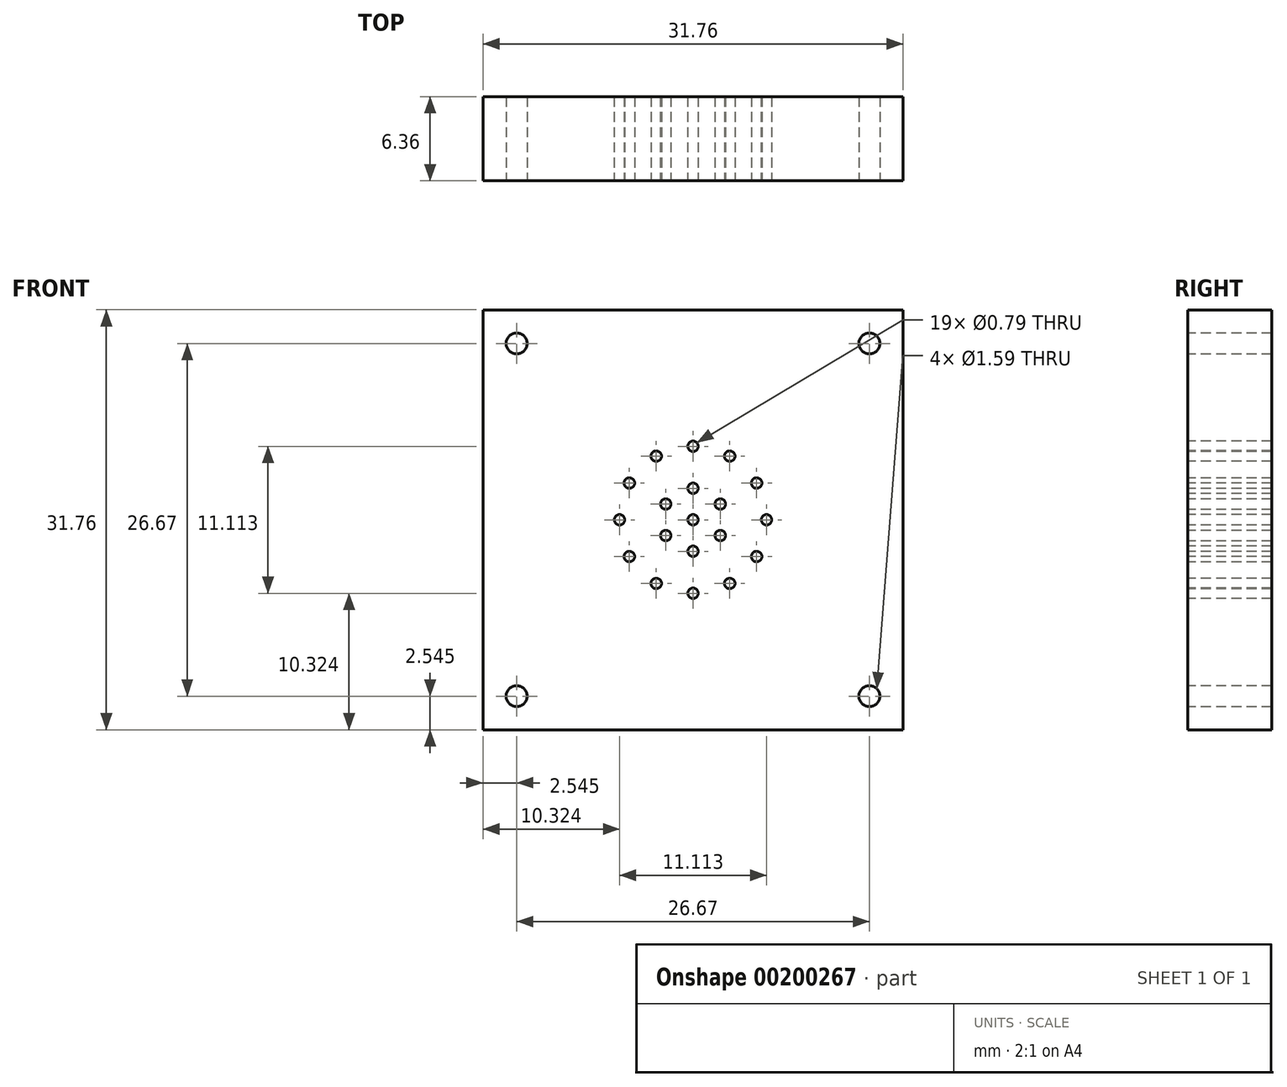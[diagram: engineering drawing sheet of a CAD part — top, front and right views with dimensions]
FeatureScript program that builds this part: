
annotation { "Feature Type Name" : "Feature", "Feature Type Description" : "" }
export const myFeature = defineFeature(function(context is Context, id is Id, definition is map)
    precondition{}
    {
        {
            var Q0;
            Q0=qCreatedBy(makeId("Front.planeOp"),FACE);
            var sketch = newSketch(context, id + "F0", { "sketchPlane" : qUnion([Q0])});
            skLineSegment(sketch, "E0.bottom", {"start": v(15.88, -15.87) * mm, "end": v(-15.88, -15.88) * mm});
            skLineSegment(sketch, "E0.top", {"start": v(15.88, 15.88) * mm, "end": v(-15.88, 15.87) * mm});
            skLineSegment(sketch, "E0.left", {"start": v(15.88, -15.88) * mm, "end": v(15.88, 15.88) * mm});
            skLineSegment(sketch, "E0.right", {"start": v(-15.88, -15.88) * mm, "end": v(-15.88, 15.87) * mm});
            skPoint(sketch, "E0.middle", {"position": v(0, 0) * mm});
            skSolve(sketch);
        }
        {
            var Q0;
            Q0=makeQuery(id+"F0.imprint","IMPRINT",FACE,{"disambiguationData":[TD([[makeQuery(id+"F0.imprint","IMPRINT",EDGE,{"derivedFrom":sQuery(id+"F0.wireOp",EDGE,"E0.bottom")}),-1.0]])]});
            extrude(context, id + "F1", {"entities" : qUnion([Q0]), "endBound" : BoundingType.SYMMETRIC, "offsetDistance" : 25.4 * mm, "depth" : 6.35 * mm});
        }
        {
            var Q0;
            Q0=makeQuery(id+"F1.opExtrude","CAP_FACE",FACE,{"disambiguationData":[OSD([sQuery(id+"F0.wireOp",EDGE,"E0.bottom"),sQuery(id+"F0.wireOp",EDGE,"E0.top"),sQuery(id+"F0.wireOp",EDGE,"E0.left"),sQuery(id+"F0.wireOp",EDGE,"E0.right")])],"isStart":false});
            var sketch = newSketch(context, id + "F2", { "sketchPlane" : qUnion([Q0])});
            skCircle(sketch, "E1", {"center": v(0, 0) * mm, "radius": 2.38 * mm});
            skCircle(sketch, "E2", {"center": v(0, 0) * mm, "radius": 5.56 * mm});
            skCircle(sketch, "E3.cCircle", {"center": v(0, 0) * mm, "radius": 2.38 * mm, "construction": true});
            skLineSegment(sketch, "E3.0", {"start": v(0, 2.38) * mm, "end": v(2.06, 1.2) * mm});
            skLineSegment(sketch, "E3.1", {"start": v(2.06, 1.2) * mm, "end": v(2.06, -1.2) * mm});
            skLineSegment(sketch, "E3.2", {"start": v(2.06, -1.2) * mm, "end": v(0, -2.38) * mm});
            skLineSegment(sketch, "E3.3", {"start": v(0, -2.38) * mm, "end": v(-2.06, -1.2) * mm});
            skLineSegment(sketch, "E3.4", {"start": v(-2.06, -1.2) * mm, "end": v(-2.06, 1.2) * mm});
            skLineSegment(sketch, "E3.5", {"start": v(-2.06, 1.2) * mm, "end": v(0, 2.38) * mm});
            skCircle(sketch, "E4.cCircle", {"center": v(0, 0) * mm, "radius": 5.56 * mm, "construction": true});
            skLineSegment(sketch, "E5.0", {"start": v(0, 5.56) * mm, "end": v(2.78, 4.81) * mm});
            skLineSegment(sketch, "E5.1", {"start": v(2.78, 4.81) * mm, "end": v(4.81, 2.78) * mm});
            skLineSegment(sketch, "E5.2", {"start": v(4.81, 2.78) * mm, "end": v(5.56, 0) * mm});
            skLineSegment(sketch, "E5.3", {"start": v(5.56, 0) * mm, "end": v(4.81, -2.78) * mm});
            skLineSegment(sketch, "E5.4", {"start": v(4.81, -2.78) * mm, "end": v(2.78, -4.81) * mm});
            skLineSegment(sketch, "E5.5", {"start": v(2.78, -4.81) * mm, "end": v(0, -5.56) * mm});
            skLineSegment(sketch, "E5.6", {"start": v(0, -5.56) * mm, "end": v(-2.78, -4.81) * mm});
            skLineSegment(sketch, "E5.7", {"start": v(-2.78, -4.81) * mm, "end": v(-4.81, -2.78) * mm});
            skLineSegment(sketch, "E5.8", {"start": v(-4.81, -2.78) * mm, "end": v(-5.56, 0) * mm});
            skLineSegment(sketch, "E5.9", {"start": v(-5.56, 0) * mm, "end": v(-4.81, 2.78) * mm});
            skLineSegment(sketch, "E5.10", {"start": v(-4.81, 2.78) * mm, "end": v(-2.78, 4.81) * mm});
            skLineSegment(sketch, "E5.11", {"start": v(-2.78, 4.81) * mm, "end": v(0, 5.56) * mm});
            skSolve(sketch);
        }
        {
            var Q0;
            Q0=sQuery(id+"F2.wireOp",VERTEX,"E1.center");
            var Q1;
            Q1=sQuery(id+"F2.wireOp",VERTEX,"E3.0.start");
            var Q2;
            Q2=sQuery(id+"F2.wireOp",VERTEX,"E3.1.start");
            var Q3;
            Q3=sQuery(id+"F2.wireOp",VERTEX,"E3.2.start");
            var Q4;
            Q4=sQuery(id+"F2.wireOp",VERTEX,"E3.3.start");
            var Q5;
            Q5=sQuery(id+"F2.wireOp",VERTEX,"E3.4.start");
            var Q6;
            Q6=sQuery(id+"F2.wireOp",VERTEX,"E3.5.start");
            var Q7;
            Q7=sQuery(id+"F2.wireOp",VERTEX,"E4.5.end");
            var Q8;
            Q8=sQuery(id+"F2.wireOp",VERTEX,"E4.1.start");
            var Q9;
            Q9=sQuery(id+"F2.wireOp",VERTEX,"E4.2.start");
            var Q10;
            Q10=sQuery(id+"F2.wireOp",VERTEX,"E4.3.start");
            var Q11;
            Q11=sQuery(id+"F2.wireOp",VERTEX,"E4.4.start");
            var Q12;
            Q12=sQuery(id+"F2.wireOp",VERTEX,"E4.5.start");
            var Q13;
            Q13=sQuery(id+"F2.wireOp",VERTEX,"E5.9.end");
            var Q14;
            Q14=sQuery(id+"F2.wireOp",VERTEX,"E5.11.start");
            var Q15;
            Q15=sQuery(id+"F2.wireOp",VERTEX,"E5.11.end");
            var Q16;
            Q16=sQuery(id+"F2.wireOp",VERTEX,"E5.1.start");
            var Q17;
            Q17=sQuery(id+"F2.wireOp",VERTEX,"E5.2.start");
            var Q18;
            Q18=sQuery(id+"F2.wireOp",VERTEX,"E5.3.start");
            var Q19;
            Q19=sQuery(id+"F2.wireOp",VERTEX,"E5.4.start");
            var Q20;
            Q20=sQuery(id+"F2.wireOp",VERTEX,"E5.5.start");
            var Q21;
            Q21=sQuery(id+"F2.wireOp",VERTEX,"E5.6.start");
            var Q22;
            Q22=sQuery(id+"F2.wireOp",VERTEX,"E5.7.start");
            var Q23;
            Q23=sQuery(id+"F2.wireOp",VERTEX,"E5.8.start");
            var Q24;
            Q24=sQuery(id+"F2.wireOp",VERTEX,"E5.8.end");
            var Q25;
            Q25=makeQuery(id+"F1.opExtrude","SWEPT_BODY",BODY,{"disambiguationData":[OSD([sQuery(id+"F0.wireOp",EDGE,"E0.bottom"),sQuery(id+"F0.wireOp",EDGE,"E0.top"),sQuery(id+"F0.wireOp",EDGE,"E0.left"),sQuery(id+"F0.wireOp",EDGE,"E0.right")])]});
            hole(context, id + "F3", {"style" : HoleStyle.SIMPLE, "endStyle" : HoleEndStyle.THROUGH, "holeDiameter" : 0.8 * mm, "locations" : qUnion([Q0, Q1, Q2, Q3, Q4, Q5, Q6, Q7, Q8, Q9, Q10, Q11, Q12, Q13, Q14, Q15, Q16, Q17, Q18, Q19, Q20, Q21, Q22, Q23, Q24]), "scope" : qUnion([Q25]), "isTappedThrough" : true});
        }
        {
            var Q0;
            Q0=makeQuery(id+"F1.opExtrude","CAP_FACE",FACE,{"disambiguationData":[OSD([sQuery(id+"F0.wireOp",EDGE,"E0.bottom"),sQuery(id+"F0.wireOp",EDGE,"E0.top"),sQuery(id+"F0.wireOp",EDGE,"E0.left"),sQuery(id+"F0.wireOp",EDGE,"E0.right")])],"isStart":false});
            var sketch = newSketch(context, id + "F4", { "sketchPlane" : qUnion([Q0])});
            skLineSegment(sketch, "E6.bottom", {"start": v(13.33, -13.34) * mm, "end": v(-13.34, -13.34) * mm});
            skLineSegment(sketch, "E6.top", {"start": v(13.34, 13.34) * mm, "end": v(-13.34, 13.33) * mm});
            skLineSegment(sketch, "E6.left", {"start": v(13.33, -13.33) * mm, "end": v(13.34, 13.33) * mm});
            skLineSegment(sketch, "E6.right", {"start": v(-13.34, -13.34) * mm, "end": v(-13.34, 13.33) * mm});
            skPoint(sketch, "E6.middle", {"position": v(0, 0) * mm});
            skSolve(sketch);
        }
        {
            var Q0;
            Q0=sQuery(id+"F4.wireOp",VERTEX,"E6.right.end");
            var Q1;
            Q1=sQuery(id+"F4.wireOp",VERTEX,"E6.bottom.end");
            var Q2;
            Q2=sQuery(id+"F4.wireOp",VERTEX,"E6.left.end");
            var Q3;
            Q3=sQuery(id+"F4.wireOp",VERTEX,"E6.left.start");
            var Q4;
            Q4=makeQuery(id+"F1.opExtrude","SWEPT_BODY",BODY,{"disambiguationData":[OSD([sQuery(id+"F0.wireOp",EDGE,"E0.bottom"),sQuery(id+"F0.wireOp",EDGE,"E0.top"),sQuery(id+"F0.wireOp",EDGE,"E0.left"),sQuery(id+"F0.wireOp",EDGE,"E0.right")])]});
            hole(context, id + "F5", {"style" : HoleStyle.SIMPLE, "endStyle" : HoleEndStyle.THROUGH, "holeDiameter" : 1.59 * mm, "majorDiameter" : 6.35 * mm, "locations" : qUnion([Q0, Q1, Q2, Q3]), "scope" : qUnion([Q4]), "isTappedThrough" : true, "tappedDepth" : 12.7 * mm, "tapClearance" : 3});
        }
    });
